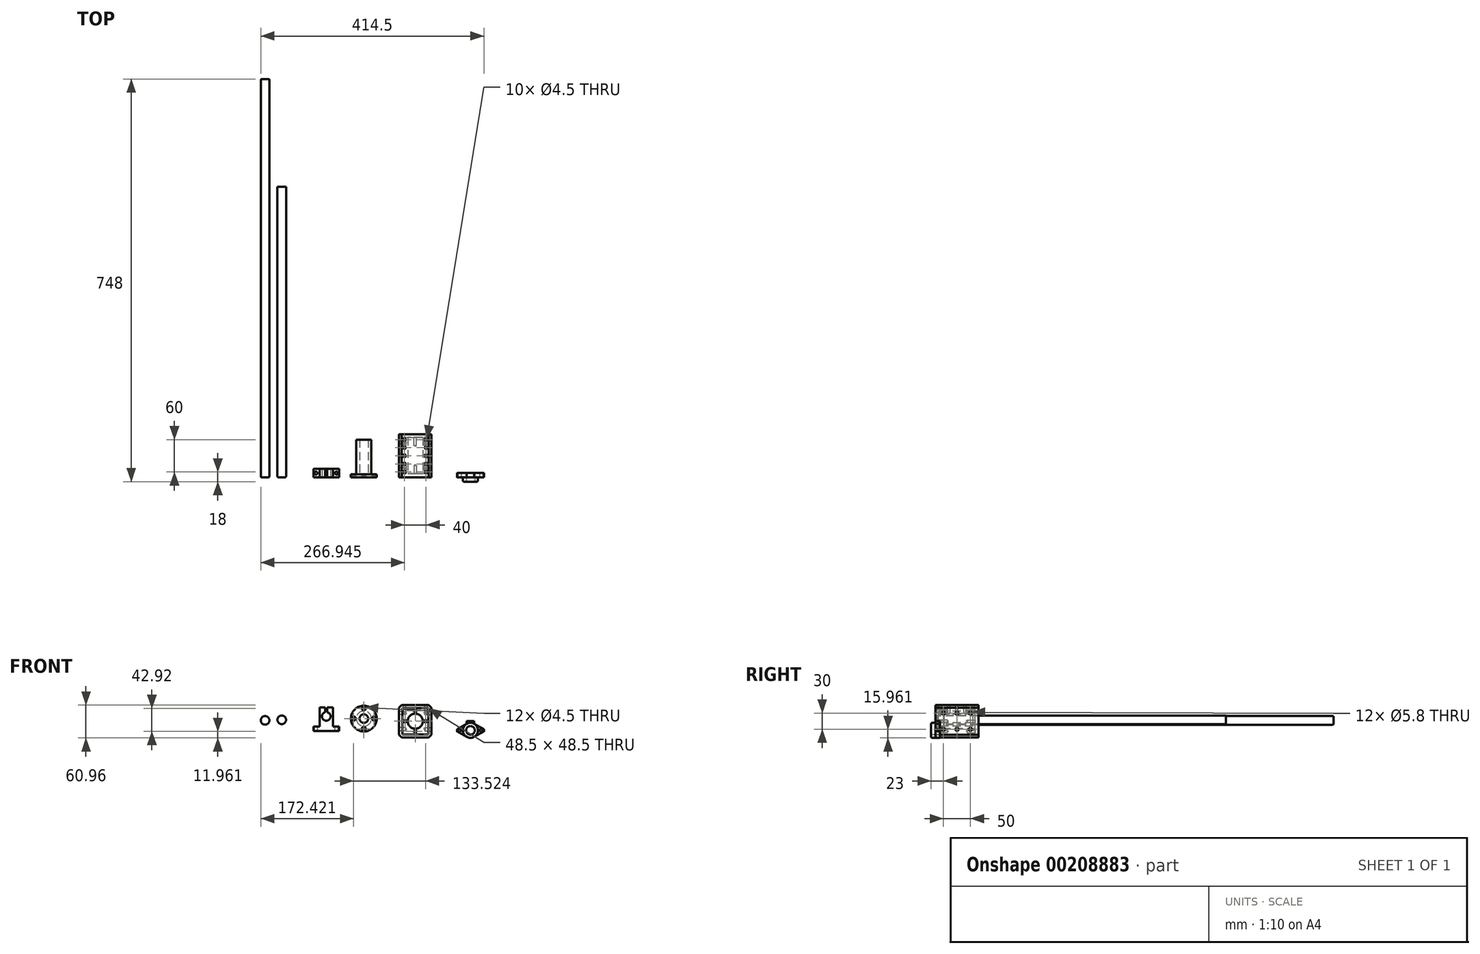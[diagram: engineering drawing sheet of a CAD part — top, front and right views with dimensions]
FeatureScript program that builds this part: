
annotation { "Feature Type Name" : "Feature", "Feature Type Description" : "" }
export const myFeature = defineFeature(function(context is Context, id is Id, definition is map)
    precondition{}
    {
        {
            var Q0;
            Q0=qCreatedBy(makeId("Front.planeOp"),FACE);
            var sketch = newSketch(context, id + "F0", { "sketchPlane" : qUnion([Q0])});
            skLineSegment(sketch, "E0.bottom", {"start": v(-58.78, 52.45) * mm, "end": v(-106.78, 52.45) * mm});
            skLineSegment(sketch, "E0.top", {"start": v(-58.78, 60.45) * mm, "end": v(-106.78, 60.45) * mm});
            skLineSegment(sketch, "E0.left", {"start": v(-58.78, 52.45) * mm, "end": v(-58.78, 60.45) * mm});
            skLineSegment(sketch, "E0.right", {"start": v(-106.78, 52.45) * mm, "end": v(-106.78, 60.45) * mm});
            skPoint(sketch, "E1.middle", {"position": v(-82.78, 52.45) * mm});
            skLineSegment(sketch, "E2.bottom", {"start": v(-70.28, 96.45) * mm, "end": v(-80.78, 96.45) * mm});
            skLineSegment(sketch, "E2.left", {"start": v(-70.28, 96.45) * mm, "end": v(-70.28, 60.45) * mm});
            skLineSegment(sketch, "E2.right", {"start": v(-95.28, 96.45) * mm, "end": v(-95.28, 60.45) * mm});
            skLineSegment(sketch, "E3", {"start": v(-82.78, 96.45) * mm, "end": v(-82.78, 52.45) * mm, "construction": true});
            skLineSegment(sketch, "E4.0", {"start": v(-58.78, 79.45) * mm, "end": v(-106.78, 79.45) * mm, "construction": true});
            skArc(sketch, "E5", {"start": v(-84.78, 87.2) * mm, "mid": v(-82.78, 71.45) * mm, "end": v(-80.78, 87.2) * mm});
            skLineSegment(sketch, "E6.0", {"start": v(-84.78, 87.2) * mm, "end": v(-84.78, 52.45) * mm, "construction": true});
            skLineSegment(sketch, "E7.0", {"start": v(-80.78, 87.2) * mm, "end": v(-80.78, 52.45) * mm, "construction": true});
            skLineSegment(sketch, "E8.trimOffspring", {"start": v(-84.78, 96.45) * mm, "end": v(-95.28, 96.45) * mm});
            skLineSegment(sketch, "E9", {"start": v(-80.78, 87.2) * mm, "end": v(-80.78, 96.45) * mm});
            skLineSegment(sketch, "E10", {"start": v(-84.78, 87.2) * mm, "end": v(-84.78, 96.45) * mm});
            skSolve(sketch);
        }
        {
            var Q0;
            Q0=makeQuery(id+"F0.imprint","IMPRINT",FACE,{"disambiguationData":[TD([[makeQuery(id+"F0.imprint","IMPRINT",EDGE,{"derivedFrom":sQuery(id+"F0.wireOp",EDGE,"E2.bottom")}),1.0]])]});
            var Q1;
            Q1=makeQuery(id+"F0.imprint","IMPRINT",FACE,{"disambiguationData":[TD([[makeQuery(id+"F0.imprint","IMPRINT",EDGE,{"derivedFrom":sQuery(id+"F0.wireOp",EDGE,"E0.bottom")}),-1.0]])]});
            extrude(context, id + "F1", {"entities" : qUnion([Q0, Q1]), "oppositeDirection" : true, "depth" : 16 * mm});
        }
        {
            var Q0;
            {var subQ0=sQuery(id+"F0.wireOp",EDGE,"E0.top");Q0=makeQuery(id+"F1.opExtrude","SWEPT_FACE",FACE,{"disambiguationData":[OSD([subQ0]),TDD([makeQuery(id+"F0.imprint","IMPRINT",EDGE,{"disambiguationData":[TD([[makeQuery(id+"F0.imprint","INTERSECT",VERTEX,{"derivedFrom":[subQ0,sQuery(id+"F0.wireOp",EDGE,"E0.right")]}),1.0]])],"derivedFrom":subQ0})])]});}
            var sketch = newSketch(context, id + "F2", { "sketchPlane" : qUnion([Q0])});
            skLineSegment(sketch, "E11", {"start": v(-106.78, 8) * mm, "end": v(-50.53, 8) * mm, "construction": true});
            skPoint(sketch, "E11.endSnap0", {"position": v(-106.78, 8) * mm});
            skLineSegment(sketch, "E12.0", {"start": v(-101.78, 16) * mm, "end": v(-101.78, 0) * mm, "construction": true});
            skLineSegment(sketch, "E13.0", {"start": v(-63.78, 16) * mm, "end": v(-63.78, 0) * mm, "construction": true});
            skCircle(sketch, "E14", {"center": v(-101.78, 8) * mm, "radius": 2.75 * mm});
            skCircle(sketch, "E15", {"center": v(-63.78, 8) * mm, "radius": 2.75 * mm});
            skSolve(sketch);
        }
        {
            var Q0;
            Q0=sQuery(id+"F2.wireOp",VERTEX,"E14.center");
            var Q1;
            Q1=sQuery(id+"F2.wireOp",VERTEX,"E15.center");
            var Q2;
            Q2=makeQuery(id+"F1.opExtrude","SWEPT_BODY",BODY,{"disambiguationData":[OSD([sQuery(id+"F0.wireOp",EDGE,"E0.bottom"),sQuery(id+"F0.wireOp",EDGE,"E0.top"),sQuery(id+"F0.wireOp",EDGE,"E0.left"),sQuery(id+"F0.wireOp",EDGE,"E0.right"),sQuery(id+"F0.wireOp",EDGE,"E2.bottom"),sQuery(id+"F0.wireOp",EDGE,"E2.left"),sQuery(id+"F0.wireOp",EDGE,"E2.right"),sQuery(id+"F0.wireOp",EDGE,"E5"),sQuery(id+"F0.wireOp",EDGE,"E8.trimOffspring"),sQuery(id+"F0.wireOp",EDGE,"E9"),sQuery(id+"F0.wireOp",EDGE,"E10")])]});
            hole(context, id + "F3", {"style" : HoleStyle.SIMPLE, "endStyle" : HoleEndStyle.THROUGH, "holeDiameter" : 5.5 * mm, "locations" : qUnion([Q0, Q1]), "scope" : qUnion([Q2]), "isTappedThrough" : true});
        }
        {
            var Q0;
            Q0=qCreatedBy(makeId("Front.planeOp"),FACE);
            var sketch = newSketch(context, id + "F4", { "sketchPlane" : qUnion([Q0])});
            skCircle(sketch, "E16", {"center": v(-196.37, 72.13) * mm, "radius": 8 * mm});
            skSolve(sketch);
        }
        {
            var Q0;
            Q0=qSketchRegion(id+"F4",true);
            extrude(context, id + "F5", {"entities" : qUnion([Q0]), "oppositeDirection" : true, "depth" : 740 * mm});
        }
        {
            var Q0;
            Q0=makeQuery(id+"F5.opExtrude","CAP_EDGE",EDGE,{"disambiguationData":[OSD([sQuery(id+"F4.wireOp",EDGE,"E16")])],"isStart":true});
            var Q1;
            Q1=makeQuery(id+"F5.opExtrude","CAP_EDGE",EDGE,{"disambiguationData":[OSD([sQuery(id+"F4.wireOp",EDGE,"E16")])],"isStart":false});
            fillet(context, id + "F6", {"entities" : qUnion([Q0, Q1]), "radius" : 2 * mm, "tangentPropagation" : true, "allowEdgeOverflow" : false});
        }
        {
            var Q0;
            Q0=qCreatedBy(makeId("Front.planeOp"),FACE);
            var sketch = newSketch(context, id + "F7", { "sketchPlane" : qUnion([Q0])});
            skCircle(sketch, "E17", {"center": v(-12.95, 75.48) * mm, "radius": 24 * mm});
            skCircle(sketch, "E18", {"center": v(-12.95, 75.48) * mm, "radius": 19 * mm, "construction": true});
            skCircle(sketch, "E19", {"center": v(-12.95, 75.48) * mm, "radius": 8 * mm});
            skLineSegment(sketch, "E20", {"start": v(-12.95, 75.48) * mm, "end": v(-12.95, 99.79) * mm, "construction": true});
            skCircle(sketch, "E21", {"center": v(-12.95, 94.48) * mm, "radius": 3.75 * mm});
            skCircle(sketch, "E22.1.0", {"center": v(6.05, 75.48) * mm, "radius": 3.75 * mm});
            skCircle(sketch, "E22.2.0", {"center": v(-12.95, 56.48) * mm, "radius": 3.75 * mm});
            skCircle(sketch, "E22.3.0", {"center": v(-31.95, 75.48) * mm, "radius": 3.75 * mm});
            skLineSegment(sketch, "E22.anchor1", {"start": v(-12.95, 75.48) * mm, "end": v(-12.95, 94.48) * mm, "construction": true});
            skLineSegment(sketch, "E22.anchor2", {"start": v(-12.95, 75.48) * mm, "end": v(-31.95, 75.48) * mm, "construction": true});
            skCircle(sketch, "E23", {"center": v(-12.95, 75.48) * mm, "radius": 14 * mm});
            skSolve(sketch);
        }
        {
            var Q0;
            Q0=makeQuery(id+"F7.imprint","IMPRINT",FACE,{"disambiguationData":[TD([[makeQuery(id+"F7.imprint","IMPRINT",EDGE,{"derivedFrom":sQuery(id+"F7.wireOp",EDGE,"E17")}),1.0]])]});
            var Q1;
            Q1=makeQuery(id+"F7.imprint","IMPRINT",FACE,{"disambiguationData":[TD([[makeQuery(id+"F7.imprint","IMPRINT",EDGE,{"derivedFrom":sQuery(id+"F7.wireOp",EDGE,"E22.1.0")}),1.0]])]});
            var Q2;
            Q2=makeQuery(id+"F7.imprint","IMPRINT",FACE,{"disambiguationData":[TD([[makeQuery(id+"F7.imprint","IMPRINT",EDGE,{"derivedFrom":sQuery(id+"F7.wireOp",EDGE,"E22.2.0")}),1.0]])]});
            var Q3;
            Q3=makeQuery(id+"F7.imprint","IMPRINT",FACE,{"disambiguationData":[TD([[makeQuery(id+"F7.imprint","IMPRINT",EDGE,{"derivedFrom":sQuery(id+"F7.wireOp",EDGE,"E22.3.0")}),1.0]])]});
            var Q4;
            Q4=makeQuery(id+"F7.imprint","IMPRINT",FACE,{"disambiguationData":[TD([[makeQuery(id+"F7.imprint","IMPRINT",EDGE,{"derivedFrom":sQuery(id+"F7.wireOp",EDGE,"E21")}),1.0]])]});
            var Q5;
            Q5=makeQuery(id+"F7.imprint","IMPRINT",FACE,{"disambiguationData":[TD([[makeQuery(id+"F7.imprint","IMPRINT",EDGE,{"derivedFrom":sQuery(id+"F7.wireOp",EDGE,"E19")}),-1.0]])]});
            extrude(context, id + "F8", {"entities" : qUnion([Q0, Q1, Q2, Q3, Q4, Q5]), "oppositeDirection" : true, "depth" : 6 * mm});
        }
        {
            var Q0;
            Q0=makeQuery(id+"F7.imprint","IMPRINT",FACE,{"disambiguationData":[TD([[makeQuery(id+"F7.imprint","IMPRINT",EDGE,{"derivedFrom":sQuery(id+"F7.wireOp",EDGE,"E19")}),-1.0]])]});
            extrude(context, id + "F9", {"entities" : qUnion([Q0]), "operationType" : NewBodyOperationType.ADD, "oppositeDirection" : true, "depth" : 70 * mm});
        }
        {
            var Q0;
            Q0=sQuery(id+"F7.wireOp",VERTEX,"E21.center");
            var Q1;
            Q1=sQuery(id+"F7.wireOp",VERTEX,"E22.1.0.center");
            var Q2;
            Q2=sQuery(id+"F7.wireOp",VERTEX,"E22.2.0.center");
            var Q3;
            Q3=sQuery(id+"F7.wireOp",VERTEX,"E22.anchor2.end");
            var Q4;
            Q4=makeQuery(id+"F8.opExtrude","SWEPT_BODY",BODY,{"disambiguationData":[OSD([sQuery(id+"F7.wireOp",EDGE,"E17"),sQuery(id+"F7.wireOp",EDGE,"E19")])]});
            hole(context, id + "F10", {"style" : HoleStyle.C_BORE, "endStyle" : HoleEndStyle.THROUGH, "holeDiameter" : 4.5 * mm, "cBoreDiameter" : 7.5 * mm, "cBoreDepth" : 4.1 * mm, "locations" : qUnion([Q0, Q1, Q2, Q3]), "scope" : qUnion([Q4]), "isTappedThrough" : true});
        }
        {
            var Q0;
            Q0=qCreatedBy(makeId("Front.planeOp"),FACE);
            var sketch = newSketch(context, id + "F11", { "sketchPlane" : qUnion([Q0])});
            skCircle(sketch, "E24", {"center": v(82.57, 70.56) * mm, "radius": 24 * mm});
            skCircle(sketch, "E25", {"center": v(82.57, 70.56) * mm, "radius": 19 * mm, "construction": true});
            skCircle(sketch, "E26", {"center": v(82.57, 70.56) * mm, "radius": 8 * mm});
            skLineSegment(sketch, "E27", {"start": v(82.57, 70.56) * mm, "end": v(82.57, 94.81) * mm, "construction": true});
            skCircle(sketch, "E28", {"center": v(82.57, 89.56) * mm, "radius": 3.75 * mm});
            skCircle(sketch, "E29.1.0", {"center": v(101.57, 70.56) * mm, "radius": 3.75 * mm});
            skCircle(sketch, "E29.2.0", {"center": v(82.57, 51.56) * mm, "radius": 3.75 * mm});
            skCircle(sketch, "E29.3.0", {"center": v(63.57, 70.56) * mm, "radius": 3.75 * mm});
            skLineSegment(sketch, "E29.anchor1", {"start": v(82.57, 70.56) * mm, "end": v(82.57, 89.56) * mm, "construction": true});
            skLineSegment(sketch, "E29.anchor2", {"start": v(82.57, 70.56) * mm, "end": v(63.57, 70.56) * mm, "construction": true});
            skCircle(sketch, "E30", {"center": v(82.57, 70.56) * mm, "radius": 14 * mm});
            skLineSegment(sketch, "E31.bottom", {"start": v(112.57, 40.56) * mm, "end": v(52.57, 40.56) * mm});
            skLineSegment(sketch, "E31.top", {"start": v(112.57, 100.56) * mm, "end": v(52.57, 100.56) * mm});
            skLineSegment(sketch, "E31.left", {"start": v(112.57, 40.56) * mm, "end": v(112.57, 100.56) * mm});
            skLineSegment(sketch, "E31.right", {"start": v(52.57, 40.56) * mm, "end": v(52.57, 100.56) * mm});
            skLineSegment(sketch, "E32.bottom", {"start": v(106.82, 94.81) * mm, "end": v(58.32, 94.81) * mm});
            skLineSegment(sketch, "E32.top", {"start": v(106.82, 46.31) * mm, "end": v(58.32, 46.31) * mm});
            skLineSegment(sketch, "E32.left", {"start": v(106.82, 94.81) * mm, "end": v(106.82, 46.31) * mm});
            skLineSegment(sketch, "E32.right", {"start": v(58.32, 94.81) * mm, "end": v(58.32, 46.31) * mm});
            skSolve(sketch);
        }
        {
            var Q0;
            Q0=makeQuery(id+"F11.imprint","IMPRINT",FACE,{"disambiguationData":[TD([[makeQuery(id+"F11.imprint","IMPRINT",EDGE,{"derivedFrom":sQuery(id+"F11.wireOp",EDGE,"E24")}),-1.0]])]});
            var Q1;
            Q1=makeQuery(id+"F11.imprint","IMPRINT",FACE,{"disambiguationData":[TD([[makeQuery(id+"F11.imprint","IMPRINT",EDGE,{"derivedFrom":sQuery(id+"F11.wireOp",EDGE,"E24")}),1.0]])]});
            var Q2;
            Q2=makeQuery(id+"F11.imprint","IMPRINT",FACE,{"disambiguationData":[TD([[makeQuery(id+"F11.imprint","IMPRINT",EDGE,{"derivedFrom":sQuery(id+"F11.wireOp",EDGE,"E28")}),1.0]])]});
            var Q3;
            Q3=makeQuery(id+"F11.imprint","IMPRINT",FACE,{"disambiguationData":[TD([[makeQuery(id+"F11.imprint","IMPRINT",EDGE,{"derivedFrom":sQuery(id+"F11.wireOp",EDGE,"E29.3.0")}),1.0]])]});
            var Q4;
            Q4=makeQuery(id+"F11.imprint","IMPRINT",FACE,{"disambiguationData":[TD([[makeQuery(id+"F11.imprint","IMPRINT",EDGE,{"derivedFrom":sQuery(id+"F11.wireOp",EDGE,"E29.2.0")}),1.0]])]});
            var Q5;
            Q5=makeQuery(id+"F11.imprint","IMPRINT",FACE,{"disambiguationData":[TD([[makeQuery(id+"F11.imprint","IMPRINT",EDGE,{"derivedFrom":sQuery(id+"F11.wireOp",EDGE,"E29.1.0")}),1.0]])]});
            var Q6;
            Q6=makeQuery(id+"F11.imprint","IMPRINT",FACE,{"disambiguationData":[TD([[makeQuery(id+"F11.imprint","IMPRINT",EDGE,{"derivedFrom":sQuery(id+"F11.wireOp",EDGE,"E31.bottom")}),-1.0]])]});
            extrude(context, id + "F12", {"entities" : qUnion([Q0, Q1, Q2, Q3, Q4, Q5, Q6]), "oppositeDirection" : true, "depth" : 80 * mm});
        }
        {
            var Q0;
            Q0=makeQuery(id+"F11.imprint","IMPRINT",FACE,{"disambiguationData":[TD([[makeQuery(id+"F11.imprint","IMPRINT",EDGE,{"derivedFrom":sQuery(id+"F11.wireOp",EDGE,"E24")}),1.0]])]});
            var Q1;
            Q1=makeQuery(id+"F11.imprint","IMPRINT",FACE,{"disambiguationData":[TD([[makeQuery(id+"F11.imprint","IMPRINT",EDGE,{"derivedFrom":sQuery(id+"F11.wireOp",EDGE,"E29.1.0")}),1.0]])]});
            var Q2;
            Q2=makeQuery(id+"F11.imprint","IMPRINT",FACE,{"disambiguationData":[TD([[makeQuery(id+"F11.imprint","IMPRINT",EDGE,{"derivedFrom":sQuery(id+"F11.wireOp",EDGE,"E28")}),1.0]])]});
            var Q3;
            Q3=makeQuery(id+"F11.imprint","IMPRINT",FACE,{"disambiguationData":[TD([[makeQuery(id+"F11.imprint","IMPRINT",EDGE,{"derivedFrom":sQuery(id+"F11.wireOp",EDGE,"E29.2.0")}),1.0]])]});
            var Q4;
            Q4=makeQuery(id+"F11.imprint","IMPRINT",FACE,{"disambiguationData":[TD([[makeQuery(id+"F11.imprint","IMPRINT",EDGE,{"derivedFrom":sQuery(id+"F11.wireOp",EDGE,"E29.3.0")}),1.0]])]});
            var Q5;
            Q5=makeQuery(id+"F11.imprint","IMPRINT",FACE,{"disambiguationData":[TD([[makeQuery(id+"F11.imprint","IMPRINT",EDGE,{"derivedFrom":sQuery(id+"F11.wireOp",EDGE,"E24")}),-1.0]])]});
            extrude(context, id + "F13", {"entities" : qUnion([Q0, Q1, Q2, Q3, Q4, Q5]), "operationType" : NewBodyOperationType.REMOVE, "oppositeDirection" : true, "depth" : 7 * mm});
        }
        {
            var Q0;
            Q0=makeQuery(id+"F13.boolean.opBoolean","COPY",FACE,{"derivedFrom":makeQuery(id+"F13.opExtrude","CAP_FACE",FACE,{"disambiguationData":[OSD([sQuery(id+"F11.wireOp",EDGE,"E24"),sQuery(id+"F11.wireOp",EDGE,"E30")])],"isStart":false})});
            var sketch = newSketch(context, id + "F14", { "sketchPlane" : qUnion([Q0])});
            skLineSegment(sketch, "E33", {"start": v(82.57, 70.56) * mm, "end": v(82.57, 94.56) * mm, "construction": true});
            skCircle(sketch, "E34", {"center": v(82.57, 70.56) * mm, "radius": 19 * mm, "construction": true});
            skCircle(sketch, "E35", {"center": v(82.57, 89.56) * mm, "radius": 2.25 * mm});
            skCircle(sketch, "E36.1.0", {"center": v(63.57, 70.56) * mm, "radius": 2.25 * mm});
            skCircle(sketch, "E36.2.0", {"center": v(82.57, 51.56) * mm, "radius": 2.25 * mm});
            skCircle(sketch, "E36.3.0", {"center": v(101.57, 70.56) * mm, "radius": 2.25 * mm});
            skSolve(sketch);
        }
        {
            var Q0;
            Q0=sQuery(id+"F14.wireOp",VERTEX,"E35.center");
            var Q1;
            Q1=sQuery(id+"F14.wireOp",VERTEX,"E36.3.0.center");
            var Q2;
            Q2=sQuery(id+"F14.wireOp",VERTEX,"E36.2.0.center");
            var Q3;
            Q3=sQuery(id+"F14.wireOp",VERTEX,"E36.1.0.center");
            var Q4;
            Q4=makeQuery(id+"F12.opExtrude","SWEPT_BODY",BODY,{"disambiguationData":[OSD([sQuery(id+"F11.wireOp",EDGE,"E30"),sQuery(id+"F11.wireOp",EDGE,"E31.bottom"),sQuery(id+"F11.wireOp",EDGE,"E31.top"),sQuery(id+"F11.wireOp",EDGE,"E31.left"),sQuery(id+"F11.wireOp",EDGE,"E31.right")])]});
            hole(context, id + "F15", {"style" : HoleStyle.SIMPLE, "endStyle" : HoleEndStyle.BLIND, "holeDiameter" : 4.5 * mm, "holeDepth" : 15 * mm, "locations" : qUnion([Q0, Q1, Q2, Q3]), "scope" : qUnion([Q4])});
        }
        {
            var Q0;
            Q0=makeQuery(id+"F12.opExtrude","CAP_FACE",FACE,{"disambiguationData":[OSD([sQuery(id+"F11.wireOp",EDGE,"E30"),sQuery(id+"F11.wireOp",EDGE,"E31.bottom"),sQuery(id+"F11.wireOp",EDGE,"E31.top"),sQuery(id+"F11.wireOp",EDGE,"E31.left"),sQuery(id+"F11.wireOp",EDGE,"E31.right")])],"isStart":false});
            var sketch = newSketch(context, id + "F16", { "sketchPlane" : qUnion([Q0])});
            skLineSegment(sketch, "E37.bottom", {"start": v(-58.32, 46.31) * mm, "end": v(-106.82, 46.31) * mm});
            skLineSegment(sketch, "E37.top", {"start": v(-58.32, 94.81) * mm, "end": v(-106.82, 94.81) * mm});
            skLineSegment(sketch, "E37.left", {"start": v(-58.32, 46.31) * mm, "end": v(-58.32, 94.81) * mm});
            skLineSegment(sketch, "E37.right", {"start": v(-106.82, 46.31) * mm, "end": v(-106.82, 94.81) * mm});
            skPoint(sketch, "E37.middle", {"position": v(-82.57, 70.56) * mm});
            skSolve(sketch);
        }
        {
            var Q0;
            Q0=makeQuery(id+"F16.imprint","IMPRINT",FACE,{"disambiguationData":[TD([[makeQuery(id+"F16.imprint","IMPRINT",EDGE,{"derivedFrom":sQuery(id+"F16.wireOp",EDGE,"E37.bottom")}),-1.0]])]});
            extrude(context, id + "F17", {"entities" : qUnion([Q0]), "operationType" : NewBodyOperationType.REMOVE, "oppositeDirection" : true, "depth" : 6 * mm});
        }
        {
            var Q0;
            Q0=makeQuery(id+"F17.boolean.opBoolean","COPY",FACE,{"derivedFrom":makeQuery(id+"F17.opExtrude","CAP_FACE",FACE,{"disambiguationData":[OSD([sQuery(id+"F11.wireOp",EDGE,"E30"),sQuery(id+"F16.wireOp",EDGE,"E37.bottom"),sQuery(id+"F16.wireOp",EDGE,"E37.top"),sQuery(id+"F16.wireOp",EDGE,"E37.left"),sQuery(id+"F16.wireOp",EDGE,"E37.right")])],"isStart":false})});
            var sketch = newSketch(context, id + "F18", { "sketchPlane" : qUnion([Q0])});
            skCircle(sketch, "E38", {"center": v(-82.57, 70.56) * mm, "radius": 19 * mm, "construction": true});
            skLineSegment(sketch, "E39", {"start": v(-82.57, 70.56) * mm, "end": v(-82.57, 94.81) * mm, "construction": true});
            skCircle(sketch, "E40", {"center": v(-82.57, 89.56) * mm, "radius": 2.74 * mm});
            skCircle(sketch, "E41.1.0", {"center": v(-101.57, 70.56) * mm, "radius": 2.74 * mm});
            skCircle(sketch, "E41.2.0", {"center": v(-82.57, 51.56) * mm, "radius": 2.74 * mm});
            skCircle(sketch, "E41.3.0", {"center": v(-63.57, 70.56) * mm, "radius": 2.74 * mm});
            skSolve(sketch);
        }
        {
            var Q0;
            Q0=sQuery(id+"F18.wireOp",VERTEX,"E40.center");
            var Q1;
            Q1=sQuery(id+"F18.wireOp",VERTEX,"E41.3.0.center");
            var Q2;
            Q2=sQuery(id+"F18.wireOp",VERTEX,"E41.2.0.center");
            var Q3;
            Q3=sQuery(id+"F18.wireOp",VERTEX,"E41.1.0.center");
            var Q4;
            Q4=makeQuery(id+"F12.opExtrude","SWEPT_BODY",BODY,{"disambiguationData":[OSD([sQuery(id+"F11.wireOp",EDGE,"E30"),sQuery(id+"F11.wireOp",EDGE,"E31.bottom"),sQuery(id+"F11.wireOp",EDGE,"E31.top"),sQuery(id+"F11.wireOp",EDGE,"E31.left"),sQuery(id+"F11.wireOp",EDGE,"E31.right")])]});
            hole(context, id + "F19", {"style" : HoleStyle.SIMPLE, "endStyle" : HoleEndStyle.BLIND, "holeDiameter" : 4.5 * mm, "holeDepth" : 15 * mm, "locations" : qUnion([Q0, Q1, Q2, Q3]), "scope" : qUnion([Q4])});
        }
        {
            var Q0;
            Q0=makeQuery(id+"F12.opExtrude","SWEPT_FACE",FACE,{"disambiguationData":[OSD([sQuery(id+"F11.wireOp",EDGE,"E31.top")])]});
            var sketch = newSketch(context, id + "F20", { "sketchPlane" : qUnion([Q0])});
            skLineSegment(sketch, "E42.bottom", {"start": v(52.57, 80) * mm, "end": v(112.57, 80) * mm});
            skLineSegment(sketch, "E42.top", {"start": v(52.57, 0) * mm, "end": v(112.57, 0) * mm});
            skLineSegment(sketch, "E42.left", {"start": v(52.57, 80) * mm, "end": v(52.57, 0) * mm});
            skLineSegment(sketch, "E42.right", {"start": v(112.57, 80) * mm, "end": v(112.57, 0) * mm});
            skLineSegment(sketch, "E43.0", {"start": v(52.57, 70) * mm, "end": v(112.57, 70) * mm, "construction": true});
            skLineSegment(sketch, "E44.0", {"start": v(62.57, 80) * mm, "end": v(62.57, 0) * mm, "construction": true});
            skCircle(sketch, "E45", {"center": v(62.57, 70) * mm, "radius": 2.75 * mm});
            skCircle(sketch, "E46.0.1.0", {"center": v(62.57, 55) * mm, "radius": 2.75 * mm});
            skCircle(sketch, "E46.0.2.0", {"center": v(62.57, 40) * mm, "radius": 2.75 * mm});
            skCircle(sketch, "E46.0.3.0", {"center": v(62.57, 25) * mm, "radius": 2.75 * mm});
            skCircle(sketch, "E46.0.4.0", {"center": v(62.57, 10) * mm, "radius": 2.75 * mm});
            skCircle(sketch, "E46.1.0.0", {"center": v(102.57, 70) * mm, "radius": 2.75 * mm});
            skCircle(sketch, "E46.1.1.0", {"center": v(102.57, 55) * mm, "radius": 2.75 * mm});
            skCircle(sketch, "E46.1.2.0", {"center": v(102.57, 40) * mm, "radius": 2.75 * mm});
            skCircle(sketch, "E46.1.3.0", {"center": v(102.57, 25) * mm, "radius": 2.75 * mm});
            skCircle(sketch, "E46.1.4.0", {"center": v(102.57, 10) * mm, "radius": 2.75 * mm});
            skLineSegment(sketch, "E46.direction1", {"start": v(62.57, 70) * mm, "end": v(102.57, 70) * mm, "construction": true});
            skLineSegment(sketch, "E46.direction2", {"start": v(62.57, 70) * mm, "end": v(62.57, 55) * mm, "construction": true});
            skSolve(sketch);
        }
        {
            var Q0;
            Q0=sQuery(id+"F20.wireOp",VERTEX,"E45.center");
            var Q1;
            Q1=sQuery(id+"F20.wireOp",VERTEX,"E46.direction2.end");
            var Q2;
            Q2=sQuery(id+"F20.wireOp",VERTEX,"E46.0.2.0.center");
            var Q3;
            Q3=sQuery(id+"F20.wireOp",VERTEX,"E46.0.3.0.center");
            var Q4;
            Q4=sQuery(id+"F20.wireOp",VERTEX,"E46.0.4.0.center");
            var Q5;
            Q5=sQuery(id+"F20.wireOp",VERTEX,"E46.1.4.0.center");
            var Q6;
            Q6=sQuery(id+"F20.wireOp",VERTEX,"E46.1.3.0.center");
            var Q7;
            Q7=sQuery(id+"F20.wireOp",VERTEX,"E46.1.2.0.center");
            var Q8;
            Q8=sQuery(id+"F20.wireOp",VERTEX,"E46.1.1.0.center");
            var Q9;
            Q9=sQuery(id+"F20.wireOp",VERTEX,"E46.direction1.end");
            var Q10;
            Q10=makeQuery(id+"F12.opExtrude","SWEPT_BODY",BODY,{"disambiguationData":[OSD([sQuery(id+"F11.wireOp",EDGE,"E30"),sQuery(id+"F11.wireOp",EDGE,"E31.bottom"),sQuery(id+"F11.wireOp",EDGE,"E31.top"),sQuery(id+"F11.wireOp",EDGE,"E31.left"),sQuery(id+"F11.wireOp",EDGE,"E31.right")])]});
            hole(context, id + "F21", {"style" : HoleStyle.SIMPLE, "endStyle" : HoleEndStyle.BLIND, "holeDiameter" : 4.5 * mm, "holeDepth" : 15 * mm, "locations" : qUnion([Q0, Q1, Q2, Q3, Q4, Q5, Q6, Q7, Q8, Q9]), "scope" : qUnion([Q10])});
        }
        {
            var Q0;
            Q0=makeQuery(id+"F12.opExtrude","SWEPT_FACE",FACE,{"disambiguationData":[OSD([sQuery(id+"F11.wireOp",EDGE,"E31.left")])]});
            var sketch = newSketch(context, id + "F22", { "sketchPlane" : qUnion([Q0])});
            skLineSegment(sketch, "E47.0", {"start": v(80, 85.56) * mm, "end": v(0, 85.56) * mm, "construction": true});
            skLineSegment(sketch, "E48.0", {"start": v(80, 55.56) * mm, "end": v(0, 55.56) * mm, "construction": true});
            skLineSegment(sketch, "E49.bottom", {"start": v(80, 100.56) * mm, "end": v(0, 100.56) * mm});
            skLineSegment(sketch, "E49.top", {"start": v(80, 40.56) * mm, "end": v(0, 40.56) * mm});
            skLineSegment(sketch, "E49.left", {"start": v(80, 100.56) * mm, "end": v(80, 40.56) * mm});
            skLineSegment(sketch, "E49.right", {"start": v(0, 100.56) * mm, "end": v(0, 40.56) * mm});
            skLineSegment(sketch, "E50.0", {"start": v(15, 100.56) * mm, "end": v(15, 40.56) * mm, "construction": true});
            skCircle(sketch, "E51", {"center": v(15, 85.56) * mm, "radius": 3 * mm});
            skCircle(sketch, "E52.0.1.0", {"center": v(15, 55.56) * mm, "radius": 3 * mm});
            skCircle(sketch, "E52.1.0.0", {"center": v(40, 85.56) * mm, "radius": 3 * mm});
            skCircle(sketch, "E52.1.1.0", {"center": v(40, 55.56) * mm, "radius": 3 * mm});
            skCircle(sketch, "E52.2.0.0", {"center": v(65, 85.56) * mm, "radius": 3 * mm});
            skCircle(sketch, "E52.2.1.0", {"center": v(65, 55.56) * mm, "radius": 3 * mm});
            skLineSegment(sketch, "E52.direction1", {"start": v(15, 85.56) * mm, "end": v(40, 85.56) * mm, "construction": true});
            skLineSegment(sketch, "E52.direction2", {"start": v(15, 85.56) * mm, "end": v(15, 55.56) * mm, "construction": true});
            skSolve(sketch);
        }
        {
            var Q0;
            Q0=sQuery(id+"F22.wireOp",VERTEX,"E51.center");
            var Q1;
            Q1=sQuery(id+"F22.wireOp",VERTEX,"E52.1.0.0.center");
            var Q2;
            Q2=sQuery(id+"F22.wireOp",VERTEX,"E52.2.0.0.center");
            var Q3;
            Q3=sQuery(id+"F22.wireOp",VERTEX,"E52.2.1.0.center");
            var Q4;
            Q4=sQuery(id+"F22.wireOp",VERTEX,"E52.1.1.0.center");
            var Q5;
            Q5=sQuery(id+"F22.wireOp",VERTEX,"E52.0.1.0.center");
            var Q6;
            Q6=makeQuery(id+"F12.opExtrude","SWEPT_BODY",BODY,{"disambiguationData":[OSD([sQuery(id+"F11.wireOp",EDGE,"E30"),sQuery(id+"F11.wireOp",EDGE,"E31.bottom"),sQuery(id+"F11.wireOp",EDGE,"E31.top"),sQuery(id+"F11.wireOp",EDGE,"E31.left"),sQuery(id+"F11.wireOp",EDGE,"E31.right")])]});
            hole(context, id + "F23", {"style" : HoleStyle.SIMPLE, "endStyle" : HoleEndStyle.BLIND, "holeDiameter" : 5.8 * mm, "holeDepth" : 12 * mm, "locations" : qUnion([Q0, Q1, Q2, Q3, Q4, Q5]), "scope" : qUnion([Q6])});
        }
        {
            var Q0;
            Q0=makeQuery(id+"F12.opExtrude","SWEPT_FACE",FACE,{"disambiguationData":[OSD([sQuery(id+"F11.wireOp",EDGE,"E31.right")])]});
            var sketch = newSketch(context, id + "F24", { "sketchPlane" : qUnion([Q0])});
            skLineSegment(sketch, "E53.bottom", {"start": v(-80, 100.56) * mm, "end": v(0, 100.56) * mm});
            skLineSegment(sketch, "E53.top", {"start": v(-80, 40.56) * mm, "end": v(0, 40.56) * mm});
            skLineSegment(sketch, "E53.left", {"start": v(-80, 100.56) * mm, "end": v(-80, 40.56) * mm});
            skLineSegment(sketch, "E53.right", {"start": v(0, 100.56) * mm, "end": v(0, 40.56) * mm});
            skLineSegment(sketch, "E54.0", {"start": v(-80, 85.56) * mm, "end": v(0, 85.56) * mm, "construction": true});
            skLineSegment(sketch, "E55.0", {"start": v(-65, 100.56) * mm, "end": v(-65, 40.56) * mm, "construction": true});
            skCircle(sketch, "E56", {"center": v(-65, 85.56) * mm, "radius": 3 * mm});
            skCircle(sketch, "E57.0.1.0", {"center": v(-65, 55.56) * mm, "radius": 3 * mm});
            skCircle(sketch, "E57.1.0.0", {"center": v(-40, 85.56) * mm, "radius": 3 * mm});
            skCircle(sketch, "E57.1.1.0", {"center": v(-40, 55.56) * mm, "radius": 3 * mm});
            skCircle(sketch, "E57.2.0.0", {"center": v(-15, 85.56) * mm, "radius": 3 * mm});
            skCircle(sketch, "E57.2.1.0", {"center": v(-15, 55.56) * mm, "radius": 3 * mm});
            skLineSegment(sketch, "E57.direction1", {"start": v(-65, 85.56) * mm, "end": v(-40, 85.56) * mm, "construction": true});
            skLineSegment(sketch, "E57.direction2", {"start": v(-65, 85.56) * mm, "end": v(-65, 55.56) * mm, "construction": true});
            skSolve(sketch);
        }
        {
            var Q0;
            Q0=sQuery(id+"F24.wireOp",VERTEX,"E57.direction1.start");
            var Q1;
            Q1=sQuery(id+"F24.wireOp",VERTEX,"E57.1.0.0.center");
            var Q2;
            Q2=sQuery(id+"F24.wireOp",VERTEX,"E57.2.0.0.center");
            var Q3;
            Q3=sQuery(id+"F24.wireOp",VERTEX,"E57.2.1.0.center");
            var Q4;
            Q4=sQuery(id+"F24.wireOp",VERTEX,"E57.1.1.0.center");
            var Q5;
            Q5=sQuery(id+"F24.wireOp",VERTEX,"E57.direction2.end");
            var Q6;
            Q6=makeQuery(id+"F12.opExtrude","SWEPT_BODY",BODY,{"disambiguationData":[OSD([sQuery(id+"F11.wireOp",EDGE,"E30"),sQuery(id+"F11.wireOp",EDGE,"E31.bottom"),sQuery(id+"F11.wireOp",EDGE,"E31.top"),sQuery(id+"F11.wireOp",EDGE,"E31.left"),sQuery(id+"F11.wireOp",EDGE,"E31.right")])]});
            hole(context, id + "F25", {"style" : HoleStyle.SIMPLE, "endStyle" : HoleEndStyle.BLIND, "holeDiameter" : 5.8 * mm, "holeDepth" : 12 * mm, "locations" : qUnion([Q0, Q1, Q2, Q3, Q4, Q5]), "scope" : qUnion([Q6])});
        }
        {
            var Q0;
            Q0=makeQuery(id+"F12.opExtrude","SWEPT_EDGE",EDGE,{"disambiguationData":[OSD([sQuery(id+"F11.wireOp",EDGE,"E31.top"),sQuery(id+"F11.wireOp",EDGE,"E31.right")])]});
            var Q1;
            Q1=makeQuery(id+"F12.opExtrude","SWEPT_EDGE",EDGE,{"disambiguationData":[OSD([sQuery(id+"F11.wireOp",EDGE,"E31.top"),sQuery(id+"F11.wireOp",EDGE,"E31.left")])]});
            var Q2;
            Q2=makeQuery(id+"F12.opExtrude","SWEPT_EDGE",EDGE,{"disambiguationData":[OSD([sQuery(id+"F11.wireOp",EDGE,"E31.bottom"),sQuery(id+"F11.wireOp",EDGE,"E31.left")])]});
            var Q3;
            Q3=makeQuery(id+"F12.opExtrude","SWEPT_EDGE",EDGE,{"disambiguationData":[OSD([sQuery(id+"F11.wireOp",EDGE,"E31.bottom"),sQuery(id+"F11.wireOp",EDGE,"E31.right")])]});
            chamfer(context, id + "F26", {"entities" : qUnion([Q0, Q1, Q2, Q3]), "width" : 5 * mm, "tangentPropagation" : true});
        }
        {
            var Q0;
            Q0=qCreatedBy(makeId("Front.planeOp"),FACE);
            var sketch = newSketch(context, id + "F27", { "sketchPlane" : qUnion([Q0])});
            skPoint(sketch, "E58.middle", {"position": v(185.13, 53.6) * mm});
            skCircle(sketch, "E59", {"center": v(185.13, 53.6) * mm, "radius": 8 * mm});
            skCircle(sketch, "E60", {"center": v(185.13, 53.6) * mm, "radius": 14 * mm});
            skLineSegment(sketch, "E61.left", {"start": v(210.13, 51.6) * mm, "end": v(210.13, 55.6) * mm});
            skLineSegment(sketch, "E61.right", {"start": v(160.13, 51.6) * mm, "end": v(160.13, 55.6) * mm});
            skCircle(sketch, "E62", {"center": v(165.13, 53.6) * mm, "radius": 2.75 * mm});
            skCircle(sketch, "E63", {"center": v(205.13, 53.6) * mm, "radius": 2.75 * mm});
            skLineSegment(sketch, "E64", {"start": v(210.13, 55.6) * mm, "end": v(192, 65.8) * mm});
            skLineSegment(sketch, "E65", {"start": v(210.13, 51.6) * mm, "end": v(192, 41.4) * mm});
            skLineSegment(sketch, "E66", {"start": v(160.13, 51.6) * mm, "end": v(178.27, 41.4) * mm});
            skLineSegment(sketch, "E67", {"start": v(160.13, 55.6) * mm, "end": v(178.27, 65.8) * mm});
            skLineSegment(sketch, "E68", {"start": v(178.27, 65.8) * mm, "end": v(178.27, 70.6) * mm});
            skLineSegment(sketch, "E69", {"start": v(192, 65.8) * mm, "end": v(192, 70.6) * mm});
            skLineSegment(sketch, "E70", {"start": v(192, 70.6) * mm, "end": v(178.27, 70.6) * mm});
            skSolve(sketch);
        }
        {
            var Q0;
            {var subQ2=sQuery(id+"F27.wireOp",EDGE,"E68");Q0=makeQuery(id+"F27.imprint","IMPRINT",FACE,{"disambiguationData":[TD([[makeQuery(id+"F27.imprint","IMPRINT",EDGE,{"derivedFrom":subQ2}),-1.0]])]});}
            var Q1;
            Q1=makeQuery(id+"F27.imprint","IMPRINT",FACE,{"disambiguationData":[TD([[makeQuery(id+"F27.imprint","IMPRINT",EDGE,{"derivedFrom":sQuery(id+"F27.wireOp",EDGE,"E61.right")}),-1.0]])]});
            var Q2;
            Q2=makeQuery(id+"F27.imprint","IMPRINT",FACE,{"disambiguationData":[TD([[makeQuery(id+"F27.imprint","IMPRINT",EDGE,{"derivedFrom":sQuery(id+"F27.wireOp",EDGE,"E59")}),-1.0]])]});
            var Q3;
            Q3=makeQuery(id+"F27.imprint","IMPRINT",FACE,{"disambiguationData":[TD([[makeQuery(id+"F27.imprint","IMPRINT",EDGE,{"derivedFrom":sQuery(id+"F27.wireOp",EDGE,"E61.left")}),1.0]])]});
            extrude(context, id + "F28", {"entities" : qUnion([Q0, Q1, Q2, Q3]), "oppositeDirection" : true, "depth" : 8 * mm});
        }
        {
            var Q0;
            Q0=makeQuery(id+"F27.imprint","IMPRINT",FACE,{"disambiguationData":[TD([[makeQuery(id+"F27.imprint","IMPRINT",EDGE,{"derivedFrom":sQuery(id+"F27.wireOp",EDGE,"E59")}),-1.0]])]});
            extrude(context, id + "F29", {"entities" : qUnion([Q0]), "operationType" : NewBodyOperationType.ADD, "depth" : 8 * mm});
        }
        {
            var Q0;
            Q0=makeQuery(id+"F29.opExtrude","CAP_EDGE",EDGE,{"disambiguationData":[OSD([sQuery(id+"F27.wireOp",EDGE,"E60")])],"isStart":false});
            fillet(context, id + "F30", {"entities" : qUnion([Q0]), "radius" : 2 * mm, "tangentPropagation" : true, "allowEdgeOverflow" : false});
        }
        {
            var Q0;
            Q0=makeQuery(id+"F28.opExtrude","CAP_EDGE",EDGE,{"disambiguationData":[OSD([sQuery(id+"F27.wireOp",EDGE,"E65")])],"isStart":true});
            var Q1;
            Q1=makeQuery(id+"F28.opExtrude","CAP_EDGE",EDGE,{"disambiguationData":[OSD([sQuery(id+"F27.wireOp",EDGE,"E64")])],"isStart":true});
            var Q2;
            Q2=makeQuery(id+"F28.opExtrude","CAP_EDGE",EDGE,{"disambiguationData":[OSD([sQuery(id+"F27.wireOp",EDGE,"E61.left")])],"isStart":true});
            var Q3;
            Q3=makeQuery(id+"F28.opExtrude","CAP_EDGE",EDGE,{"disambiguationData":[OSD([sQuery(id+"F27.wireOp",EDGE,"E66")])],"isStart":true});
            var Q4;
            Q4=makeQuery(id+"F28.opExtrude","CAP_EDGE",EDGE,{"disambiguationData":[OSD([sQuery(id+"F27.wireOp",EDGE,"E67")])],"isStart":true});
            var Q5;
            Q5=makeQuery(id+"F28.opExtrude","CAP_EDGE",EDGE,{"disambiguationData":[OSD([sQuery(id+"F27.wireOp",EDGE,"E61.right")])],"isStart":true});
            fillet(context, id + "F31", {"entities" : qUnion([Q0, Q1, Q2, Q3, Q4, Q5]), "radius" : 1 * mm, "tangentPropagation" : true, "allowEdgeOverflow" : false});
        }
        {
            var Q0;
            Q0=qCreatedBy(makeId("Front.planeOp"),FACE);
            var sketch = newSketch(context, id + "F32", { "sketchPlane" : qUnion([Q0])});
            skCircle(sketch, "E71", {"center": v(-165.51, 73.12) * mm, "radius": 8 * mm});
            skSolve(sketch);
        }
        {
            var Q0;
            Q0=makeQuery(id+"F32.imprint","IMPRINT",FACE,{"disambiguationData":[TD([[makeQuery(id+"F32.imprint","IMPRINT",EDGE,{"derivedFrom":sQuery(id+"F32.wireOp",EDGE,"E71")}),1.0]])]});
            extrude(context, id + "F33", {"entities" : qUnion([Q0]), "oppositeDirection" : true, "depth" : 540 * mm});
        }
        {
            var Q0;
            Q0=makeQuery(id+"F33.opExtrude","CAP_EDGE",EDGE,{"disambiguationData":[OSD([sQuery(id+"F32.wireOp",EDGE,"E71")])],"isStart":true});
            fillet(context, id + "F34", {"entities" : qUnion([Q0]), "radius" : 2 * mm, "tangentPropagation" : true, "allowEdgeOverflow" : false});
        }
    });
